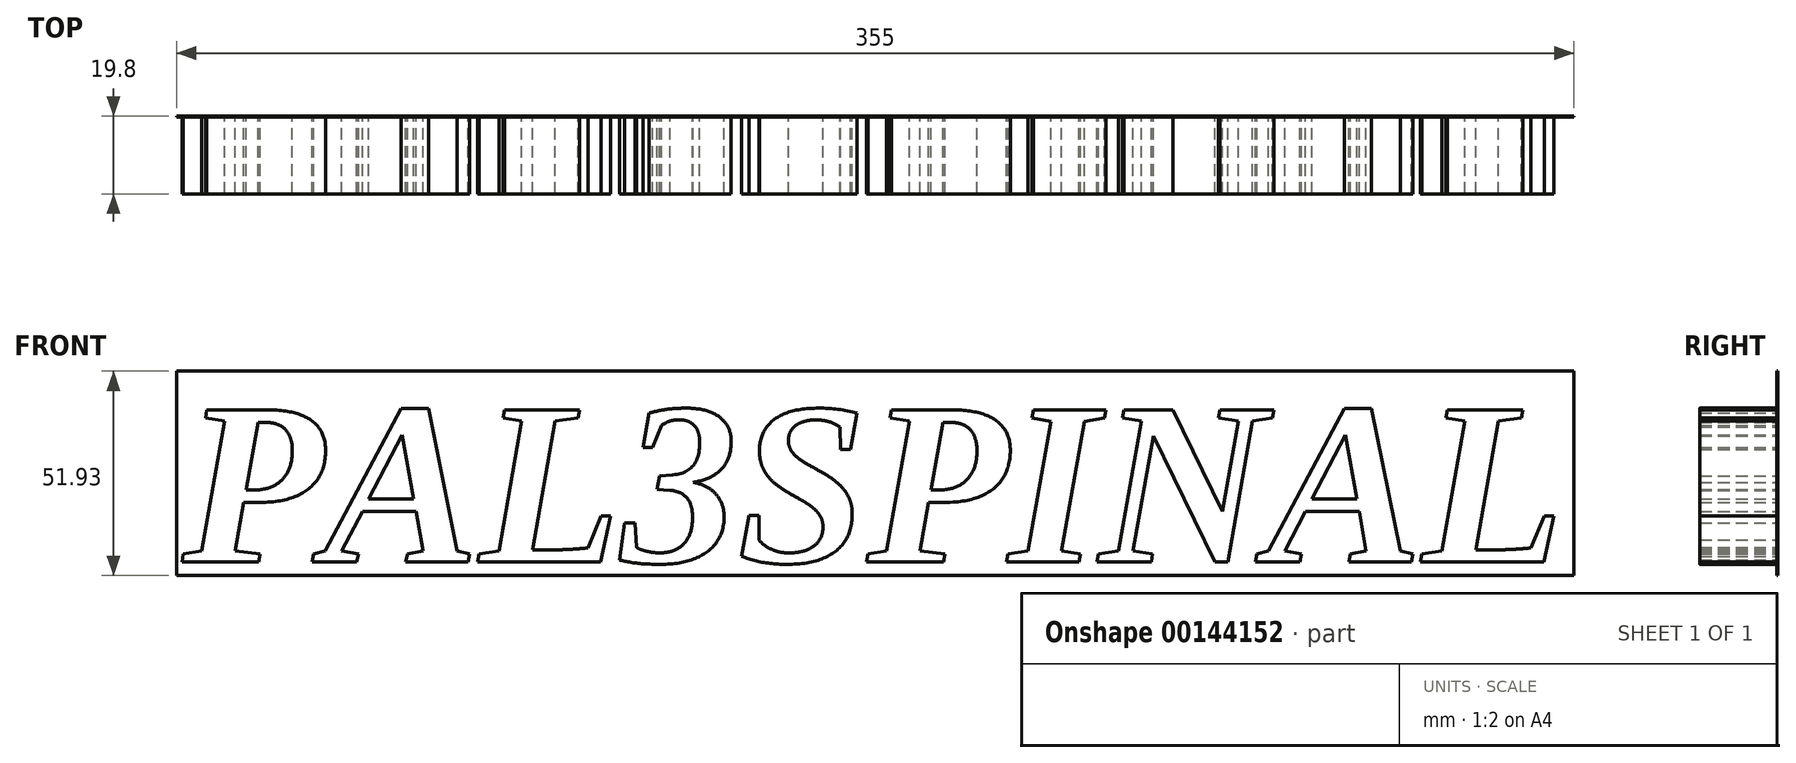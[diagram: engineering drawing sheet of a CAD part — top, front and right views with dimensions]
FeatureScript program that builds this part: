
annotation { "Feature Type Name" : "Feature", "Feature Type Description" : "" }
export const myFeature = defineFeature(function(context is Context, id is Id, definition is map)
    precondition{}
    {
        {
            var Q0;
            Q0=qCreatedBy(makeId("Front.planeOp"),FACE);
            var sketch = newSketch(context, id + "F0", { "sketchPlane" : qUnion([Q0])});
            skText(sketch, "E0", { "text": "PAL3SPINAL", "fontName": "Tinos-BoldItalic.ttf"});
            const initialGuessF0  = {"E0": [-0.0759, 0.0034, 1, 0, 0.04253]};
            skSetInitialGuess(sketch, initialGuessF0);
            skSolve(sketch);
        }
        {
            var Q0;
            Q0 = qSketchRegion(id + "F0", true);
            extrude(context, id + "F1", {"entities" : qUnion([Q0]), "depth" : 19.8 * mm});
        }
        {
            var Q0;
            Q0=qCreatedBy(makeId("Front.planeOp"),FACE);
            var sketch = newSketch(context, id + "F2", { "sketchPlane" : qUnion([Q0])});
            skLineSegment(sketch, "E1.bottom", {"start": v(277.67, 51.93) * mm, "end": v(-77.33, 51.93) * mm});
            skLineSegment(sketch, "E1.top", {"start": v(277.67, 0) * mm, "end": v(-77.33, 0) * mm});
            skLineSegment(sketch, "E1.left", {"start": v(277.67, 51.93) * mm, "end": v(277.67, 0) * mm});
            skLineSegment(sketch, "E1.right", {"start": v(-77.33, 51.93) * mm, "end": v(-77.33, 0) * mm});
            skSolve(sketch);
        }
        {
            var Q0;
            Q0 = qSketchRegion(id + "F2", true);
            extrude(context, id + "F3", {"entities" : qUnion([Q0]), "operationType" : NewBodyOperationType.ADD, "depth" : 0.25 * mm});
        }
    });
